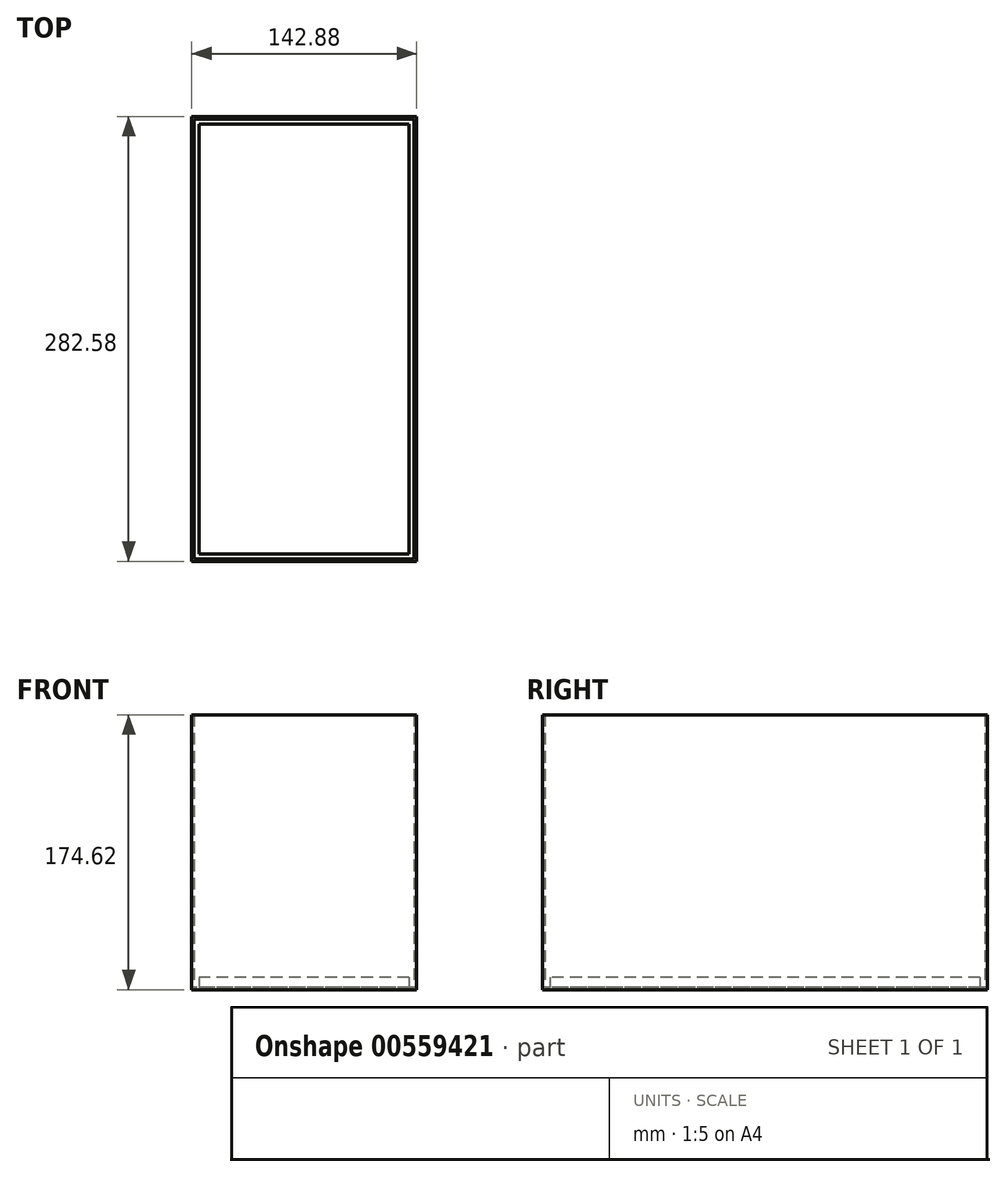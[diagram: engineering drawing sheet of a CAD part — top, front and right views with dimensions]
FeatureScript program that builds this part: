
annotation { "Feature Type Name" : "Feature", "Feature Type Description" : "" }
export const myFeature = defineFeature(function(context is Context, id is Id, definition is map)
    precondition{}
    {
        {
            var Q0;
            Q0=qCreatedBy(makeId("Top.planeOp"),FACE);
            var sketch = newSketch(context, id + "F0", { "sketchPlane" : qUnion([Q0])});
            skLineSegment(sketch, "E0.bottom", {"start": v(71.44, 141.29) * mm, "end": v(-71.44, 141.29) * mm});
            skLineSegment(sketch, "E0.top", {"start": v(71.44, -141.29) * mm, "end": v(-71.44, -141.29) * mm});
            skLineSegment(sketch, "E0.left", {"start": v(71.44, 141.29) * mm, "end": v(71.44, -141.29) * mm});
            skLineSegment(sketch, "E0.right", {"start": v(-71.44, 141.29) * mm, "end": v(-71.44, -141.29) * mm});
            skPoint(sketch, "E0.middle", {"position": v(0, 0) * mm});
            skSolve(sketch);
        }
        {
            var Q0;
            Q0 = qSketchRegion(id + "F0", true);
            extrude(context, id + "F1", {"entities" : qUnion([Q0]), "depth" : 174.62 * mm, "offsetDistance" : 25.4 * mm});
        }
        {
            var Q0;
            Q0=makeQuery(id+"F1.opExtrude","CAP_FACE",FACE,{"disambiguationData":[OSD([sQuery(id+"F0.wireOp",EDGE,"E0.bottom"),sQuery(id+"F0.wireOp",EDGE,"E0.top"),sQuery(id+"F0.wireOp",EDGE,"E0.left"),sQuery(id+"F0.wireOp",EDGE,"E0.right")])],"isStart":false});
            shell(context, id + "F2", {"entities" : qUnion([Q0]), "thickness" : 1.59 * mm});
        }
        {
            var Q0;
            Q0=makeQuery(id+"F2.opShell","OFFSET_FACE",FACE,{"disambiguationData":[OSD([sQuery(id+"F0.wireOp",EDGE,"E0.bottom"),sQuery(id+"F0.wireOp",EDGE,"E0.top"),sQuery(id+"F0.wireOp",EDGE,"E0.left"),sQuery(id+"F0.wireOp",EDGE,"E0.right")])]});
            var sketch = newSketch(context, id + "F3", { "sketchPlane" : qUnion([Q0])});
            skLineSegment(sketch, "E1.0", {"start": v(66.68, 136.53) * mm, "end": v(-66.67, 136.53) * mm});
            skLineSegment(sketch, "E1.1", {"start": v(66.68, 136.53) * mm, "end": v(66.67, -136.53) * mm});
            skLineSegment(sketch, "E1.2", {"start": v(66.67, -136.53) * mm, "end": v(-66.68, -136.53) * mm});
            skLineSegment(sketch, "E1.3", {"start": v(-66.67, 136.53) * mm, "end": v(-66.68, -136.53) * mm});
            skSolve(sketch);
        }
        {
            var Q0;
            Q0 = qSketchRegion(id + "F3", true);
            extrude(context, id + "F4", {"entities" : qUnion([Q0]), "operationType" : NewBodyOperationType.ADD, "depth" : 6.35 * mm, "offsetDistance" : 25.4 * mm});
        }
    });
